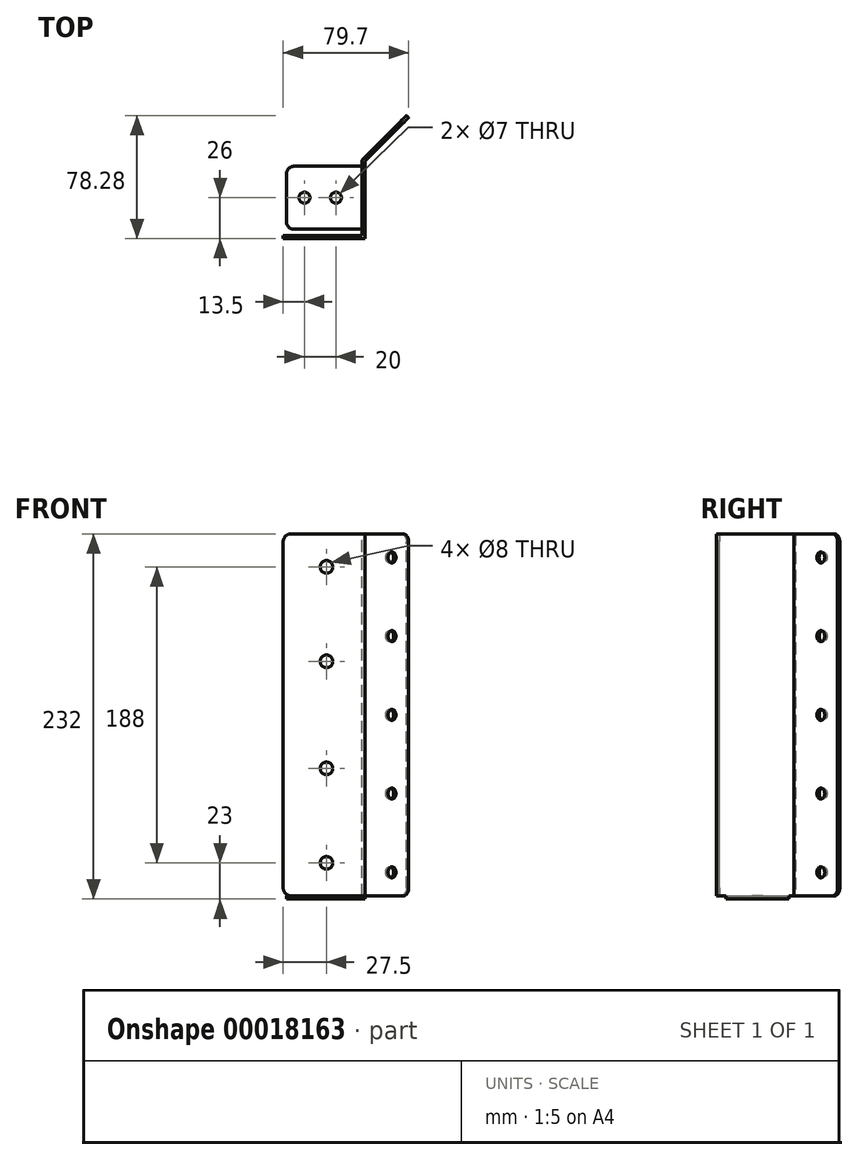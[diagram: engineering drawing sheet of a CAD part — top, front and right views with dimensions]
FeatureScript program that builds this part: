
annotation { "Feature Type Name" : "Feature", "Feature Type Description" : "" }
export const myFeature = defineFeature(function(context is Context, id is Id, definition is map)
    precondition{}
    {
        {
            var Q0;
            Q0=qCreatedBy(makeId("Front.planeOp"),FACE);
            var sketch = newSketch(context, id + "F0", { "sketchPlane" : qUnion([Q0])});
            skLineSegment(sketch, "E0.bottom", {"start": v(0, -115) * mm, "end": v(-45, -115) * mm});
            skLineSegment(sketch, "E0.top", {"start": v(0, 115) * mm, "end": v(-45, 115) * mm});
            skLineSegment(sketch, "E0.left", {"start": v(0, -115) * mm, "end": v(0, 115) * mm});
            skLineSegment(sketch, "E0.right", {"start": v(-50, -110) * mm, "end": v(-50, 110) * mm});
            skLineSegment(sketch, "E1", {"start": v(0, 0) * mm, "end": v(-144.9, 0) * mm, "construction": true});
            skPoint(sketch, "E2.visualSharp", {"position": v(-50, 115) * mm});
            skArc(sketch, "E2.filletArc", {"start": v(-45, 115) * mm, "mid": v(-48.54, 113.54) * mm, "end": v(-50, 110) * mm});
            skPoint(sketch, "E3.visualSharp", {"position": v(-50, -115) * mm});
            skArc(sketch, "E3.filletArc", {"start": v(-50, -110) * mm, "mid": v(-48.54, -113.54) * mm, "end": v(-45, -115) * mm});
            skLineSegment(sketch, "E4", {"start": v(-22.5, 115) * mm, "end": v(-22.5, -115) * mm, "construction": true});
            skCircle(sketch, "E5", {"center": v(-22.5, 34) * mm, "radius": 4 * mm});
            skCircle(sketch, "E6", {"center": v(-22.5, 94) * mm, "radius": 4 * mm});
            skCircle(sketch, "E7.MirrorC", {"center": v(-22.5, -34) * mm, "radius": 4 * mm});
            skCircle(sketch, "E8.MirrorC", {"center": v(-22.5, -94) * mm, "radius": 4 * mm});
            skSolve(sketch);
        }
        {
            var Q0;
            Q0=qSketchRegion(id+"F0",true);
            extrude(context, id + "F1", {"entities" : qUnion([Q0]), "depth" : 2 * mm});
        }
        {
            var Q0;
            Q0=makeQuery(id+"F1.opExtrude","SWEPT_FACE",FACE,{"disambiguationData":[OSD([sQuery(id+"F0.wireOp",EDGE,"E0.left")])]});
            var sketch = newSketch(context, id + "F2", { "sketchPlane" : qUnion([Q0])});
            skLineSegment(sketch, "E9.bottom", {"start": v(-2, 115) * mm, "end": v(48, 115) * mm});
            skLineSegment(sketch, "E9.top", {"start": v(-2, -115) * mm, "end": v(48, -115) * mm});
            skLineSegment(sketch, "E9.left", {"start": v(-2, 115) * mm, "end": v(-2, -115) * mm});
            skLineSegment(sketch, "E9.right", {"start": v(48, 115) * mm, "end": v(48, -115) * mm});
            skSolve(sketch);
        }
        {
            var Q0;
            Q0=qSketchRegion(id+"F2",true);
            extrude(context, id + "F3", {"entities" : qUnion([Q0]), "operationType" : NewBodyOperationType.ADD, "depth" : 2 * mm});
        }
        {
            var Q0;
            Q0=makeQuery(id+"F3.opExtrude","CAP_EDGE",EDGE,{"disambiguationData":[OSD([sQuery(id+"F2.wireOp",EDGE,"E9.right")])],"isStart":true});
            cPlane(context, id + "F4", {"entities" : qUnion([Q0]), "cplaneType" : CPlaneType.LINE_ANGLE, "offset" : 152.4 * mm, "angle" : 45 * degree, "width" : 152.4 * mm, "height" : 152.4 * mm});
        }
        {
            var Q0;
            Q0=makeQuery(id+"F3.boolean.opBoolean","MERGE",FACE,{"derivedFrom":[makeQuery(id+"F1.opExtrude","SWEPT_FACE",FACE,{"disambiguationData":[OSD([sQuery(id+"F0.wireOp",EDGE,"E0.bottom")])]}),makeQuery(id+"F3.opExtrude","SWEPT_FACE",FACE,{"disambiguationData":[OSD([sQuery(id+"F2.wireOp",EDGE,"E9.top")])]})]});
            var sketch = newSketch(context, id + "F5", { "sketchPlane" : qUnion([Q0])});
            skLineSegment(sketch, "E10.bottom", {"start": v(2, -4) * mm, "end": v(-43, -4) * mm});
            skLineSegment(sketch, "E10.top", {"start": v(2, -44) * mm, "end": v(-43, -44) * mm});
            skLineSegment(sketch, "E10.left", {"start": v(2, -4) * mm, "end": v(2, -44) * mm});
            skLineSegment(sketch, "E10.right", {"start": v(-48, -9) * mm, "end": v(-48, -39) * mm});
            skPoint(sketch, "E11.visualSharp", {"position": v(-48, -4) * mm});
            skArc(sketch, "E11.filletArc", {"start": v(-43, -4) * mm, "mid": v(-46.54, -5.46) * mm, "end": v(-48, -9) * mm});
            skPoint(sketch, "E12.visualSharp", {"position": v(-48, -44) * mm});
            skArc(sketch, "E12.filletArc", {"start": v(-48, -39) * mm, "mid": v(-46.54, -42.54) * mm, "end": v(-43, -44) * mm});
            skCircle(sketch, "E13", {"center": v(-16.5, -24) * mm, "radius": 3.5 * mm});
            skCircle(sketch, "E14", {"center": v(-36.5, -24) * mm, "radius": 3.5 * mm});
            skLineSegment(sketch, "E15", {"start": v(-48, -24) * mm, "end": v(-7.46, -24) * mm, "construction": true});
            skSolve(sketch);
        }
        {
            var Q0;
            Q0=qSketchRegion(id+"F5",true);
            extrude(context, id + "F6", {"entities" : qUnion([Q0]), "operationType" : NewBodyOperationType.ADD, "depth" : 2 * mm});
        }
        {
            var Q0;
            Q0=qCreatedBy(id+"F4.planeOp",FACE);
            var sketch = newSketch(context, id + "F7", { "sketchPlane" : qUnion([Q0])});
            skLineSegment(sketch, "E16.bottom", {"start": v(-33.94, -115) * mm, "end": v(-68.94, -115) * mm});
            skLineSegment(sketch, "E16.top", {"start": v(-33.94, 115) * mm, "end": v(-68.94, 115) * mm});
            skLineSegment(sketch, "E16.left", {"start": v(-33.94, -115) * mm, "end": v(-33.94, 115) * mm});
            skLineSegment(sketch, "E16.right", {"start": v(-73.94, -110) * mm, "end": v(-73.94, 110) * mm});
            skPoint(sketch, "E17.visualSharp", {"position": v(-73.94, 115) * mm});
            skArc(sketch, "E17.filletArc", {"start": v(-68.94, 115) * mm, "mid": v(-72.48, 113.54) * mm, "end": v(-73.94, 110) * mm});
            skPoint(sketch, "E18.visualSharp", {"position": v(-73.94, -115) * mm});
            skArc(sketch, "E18.filletArc", {"start": v(-73.94, -110) * mm, "mid": v(-72.48, -113.54) * mm, "end": v(-68.94, -115) * mm});
            skLineSegment(sketch, "E19", {"start": v(-73.94, 0) * mm, "end": v(-33.94, 0) * mm, "construction": true});
            skLineSegment(sketch, "E20", {"start": v(-58.94, 101.96) * mm, "end": v(-58.94, -121) * mm, "construction": true});
            skCircle(sketch, "E21", {"center": v(-58.94, -100) * mm, "radius": 3.5 * mm});
            skCircle(sketch, "E22.0.1.0", {"center": v(-58.94, -50) * mm, "radius": 3.5 * mm});
            skLineSegment(sketch, "E22.direction1", {"start": v(-58.94, -100) * mm, "end": v(-42.61, -100) * mm, "construction": true});
            skLineSegment(sketch, "E22.direction2", {"start": v(-58.94, -100) * mm, "end": v(-58.94, -50) * mm, "construction": true});
            skCircle(sketch, "E23.0.0.2", {"center": v(-58.94, 0) * mm, "radius": 3.5 * mm});
            skCircle(sketch, "E24.0.0.3", {"center": v(-58.94, 50) * mm, "radius": 3.5 * mm});
            skCircle(sketch, "E24.0.0.4", {"center": v(-58.94, 100) * mm, "radius": 3.5 * mm});
            skSolve(sketch);
        }
        {
            var Q0;
            Q0 = qSketchRegion(id + "F7", true);
            extrude(context, id + "F8", {"entities" : qUnion([Q0]), "operationType" : NewBodyOperationType.ADD, "oppositeDirection" : true, "depth" : 2 * mm});
        }
    });
